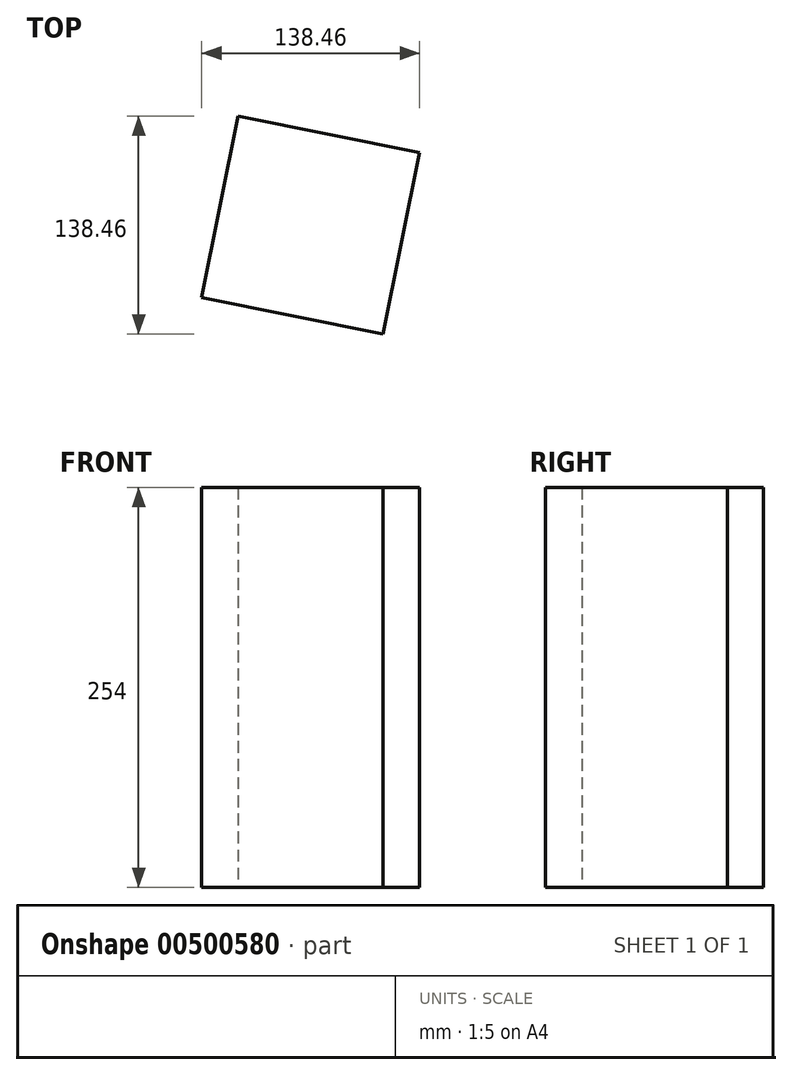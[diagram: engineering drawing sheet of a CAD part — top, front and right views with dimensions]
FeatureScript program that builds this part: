
annotation { "Feature Type Name" : "Feature", "Feature Type Description" : "" }
export const myFeature = defineFeature(function(context is Context, id is Id, definition is map)
    precondition{}
    {
        {
            var Q0;
            Q0=qCreatedBy(makeId("Top.planeOp"),FACE);
            var sketch = newSketch(context, id + "F0", { "sketchPlane" : qUnion([Q0])});
            skPoint(sketch, "E0", {"position": v(0, 0) * mm});
            skPoint(sketch, "E1", {"position": v(0.88, 0) * mm});
            skPoint(sketch, "E2", {"position": v(-9.91, 0) * mm});
            skCircle(sketch, "E3.cCircle", {"center": v(-9.91, 0) * mm, "radius": 83.14 * mm, "construction": true});
            skLineSegment(sketch, "E3.0", {"start": v(-55.96, 69.23) * mm, "end": v(59.32, 46.05) * mm});
            skLineSegment(sketch, "E3.1", {"start": v(59.32, 46.05) * mm, "end": v(36.14, -69.23) * mm});
            skLineSegment(sketch, "E3.2", {"start": v(36.14, -69.23) * mm, "end": v(-79.14, -46.05) * mm});
            skLineSegment(sketch, "E3.3", {"start": v(-79.14, -46.05) * mm, "end": v(-55.96, 69.23) * mm});
            skSolve(sketch);
        }
        {
            var Q0;
            Q0 = qSketchRegion(id + "F0", true);
            extrude(context, id + "F1", {"entities" : qUnion([Q0]), "depth" : 254 * mm});
        }
    });
